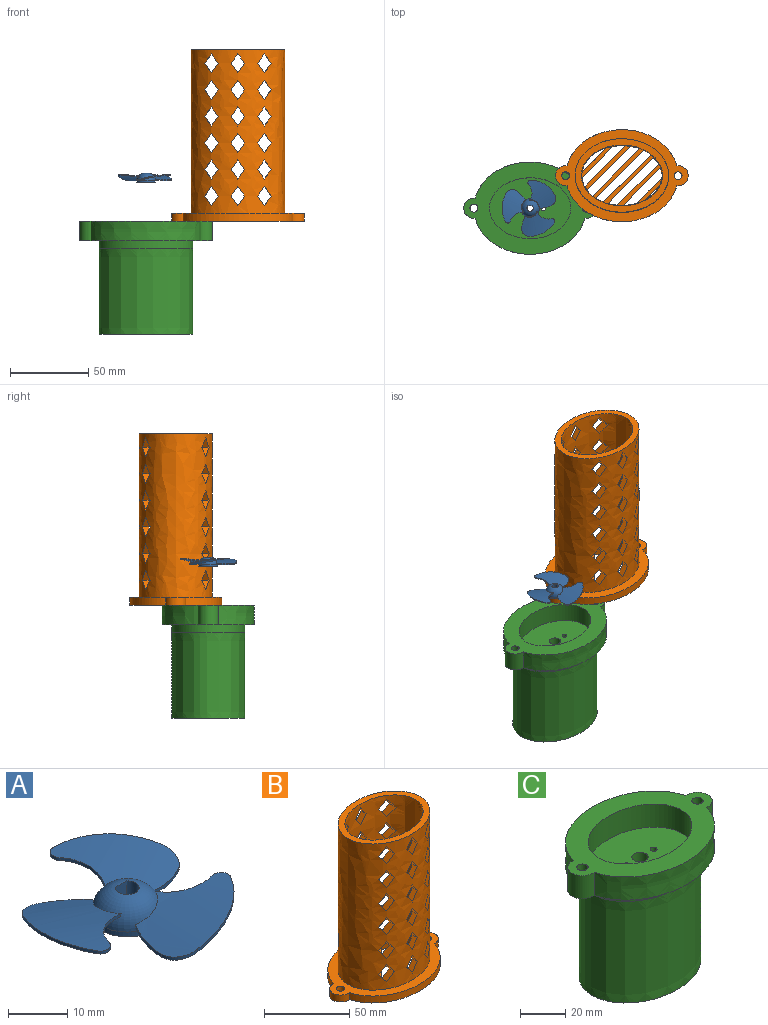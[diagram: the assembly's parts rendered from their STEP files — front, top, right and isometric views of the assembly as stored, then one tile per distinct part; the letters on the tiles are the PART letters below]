
ASSEMBLY  parts=3 mates=2
PART A: 26 faces, bbox 41.7x40.5x6 mm
  f0: cylinder r=72.3mm len=20.98mm, axis (0,-1,0), area 213.4mm2, adj f4,f5,f6,f7,f8,f23
  f1: cylinder r=71.7mm len=20.98mm, axis (0,-1,0), area 211mm2, adj f4,f5,f6,f7,f8,f23
  f2: cylinder r=6mm len=12mm, axis (0,0,-1), area 37.7mm2, adj f3,f23
  f3: plane 12x12mm, normal (0,0,-1), area 101.6mm2, adj f2,f24,f25
  f4: cylinder r=7.76mm len=9.01mm, axis (0,0,-1), area 6.5mm2, adj f0,f1,f8,f23
  f5: cylinder r=17.15mm len=8.45mm, axis (0,0,-1), area 5.5mm2, adj f0,f1,f6,f23
  f6: cylinder r=4.5mm len=4.53mm, axis (0,0,-1), area 4.3mm2, adj f0,f1,f5,f7
  f7: cylinder r=18mm len=16.51mm, axis (0,0,-1), area 11.9mm2, adj f0,f1,f6,f8
  f8: cylinder r=1.74mm len=2.64mm, axis (0,0,-1), area 2.5mm2, adj f0,f1,f4,f7
  f9: cylinder r=18mm len=18.61mm, axis (0,0,-1), area 11.9mm2, adj f10,f11,f14,f15
  f10: cylinder r=1.74mm len=3.19mm, axis (0,0,-1), area 2.5mm2, adj f9,f13,f14,f15
  f11: cylinder r=4.5mm len=6.04mm, axis (0,0,-1), area 4.3mm2, adj f9,f12,f14,f15
  f12: cylinder r=17.15mm len=6.23mm, axis (0,0,-1), area 5.5mm2, adj f11,f14,f15,f23
  f13: cylinder r=7.76mm len=8.49mm, axis (0,0,-1), area 6.5mm2, adj f10,f14,f15,f23
  f14: cylinder r=71.7mm len=25.87mm, axis (-0.87,0.5,0), area 211mm2, adj f9,f10,f11,f12,f13,f23
  f15: cylinder r=72.3mm len=26.1mm, axis (-0.87,0.5,0), area 213.4mm2, adj f9,f10,f11,f12,f13,f23
  f16: cylinder r=72.3mm len=26.1mm, axis (0.87,0.5,0), area 213.4mm2, adj f18,f19,f20,f21,f22,f23
  f17: cylinder r=71.7mm len=25.87mm, axis (0.87,0.5,0), area 211mm2, adj f18,f19,f20,f21,f22,f23
  f18: cylinder r=7.76mm len=10.11mm, axis (0,0,-1), area 6.5mm2, adj f16,f17,f22,f23
  f19: cylinder r=17.15mm len=8.48mm, axis (0,0,-1), area 5.5mm2, adj f16,f17,f20,f23
  f20: cylinder r=4.5mm len=5.92mm, axis (0,0,-1), area 4.3mm2, adj f16,f17,f19,f21
  f21: cylinder r=18mm len=15.73mm, axis (0,0,-1), area 11.9mm2, adj f16,f17,f20,f22
  f22: cylinder r=1.74mm len=2.93mm, axis (0,0,-1), area 2.5mm2, adj f16,f17,f18,f21
  f23: torus R=1mm, axis (0,0,1), area 180mm2, adj f0,f1,f2,f4,f5,f12,f13,f14
  f24: plane 5.98x2.76mm, normal (0,-1,0), area 16.4mm2, adj f3,f23,f25
  f25: cylinder r=2mm len=5.9mm, axis (0,0,-1), area 56.2mm2, adj f3,f23,f24
PART B: 193 faces, bbox 85.3x59.3x110.3 mm
  f0: plane 4.56x1.05mm, normal (0,0,-1), area 0mm2, adj f8,f172,f185
  f1: plane 4.25x3.38mm, normal (0,0,-1), area 0.2mm2, adj f8,f173,f174,f185
  f2: plane 4.96x2.58mm, normal (0,0,-1), area 0.1mm2, adj f8,f169,f170,f184
  f3: plane 4.7x2.93mm, normal (0,0,-1), area 0.2mm2, adj f8,f170,f171,f184
  f4: plane 3.89x3.75mm, normal (0,0,-1), area 0.2mm2, adj f8,f166,f167,f183
  f5: plane 5.96x1.65mm, normal (0,0,-1), area 0.1mm2, adj f8,f167,f168
  f6: plane 16.21x16.21mm, normal (0,0,-1), area 0.6mm2, adj f8,f162,f181
  f7: plane 10.43x10.43mm, normal (0,0,-1), area 0.4mm2, adj f8,f161,f190
  f8: extruded ~105x52mm, area 12884.8mm2, adj f0,f1,f2,f3,f4,f5,f6,f7
  f9: extruded ~105x60mm, area 15620.5mm2, adj f10,f11,f12,f13,f14,f15,f16,f17
  f10: plane 60x47mm, normal (0,0,1), area 624.8mm2, adj f8,f9
  f11: plane 6.17x4.33mm, normal (-0.82,0,-0.57), area 30.1mm2, adj f8,f9,f12,f14
  f12: plane 6.17x4.33mm, normal (-0.82,0,0.57), area 30.1mm2, adj f8,f9,f11,f13
  f13: plane 6.17x4.33mm, normal (0.82,0,0.57), area 30.1mm2, adj f8,f9,f12,f14
  f14: plane 6.17x4.33mm, normal (0.82,0,-0.57), area 30.1mm2, adj f8,f9,f11,f13
  f15: plane 6.17x4.33mm, normal (0.82,0,-0.57), area 30.1mm2, adj f8,f9,f16,f18
  f16: plane 6.17x4.33mm, normal (0.82,0,0.57), area 30.1mm2, adj f8,f9,f15,f17
  f17: plane 6.17x4.33mm, normal (-0.82,0,0.57), area 30.1mm2, adj f8,f9,f16,f18
  f18: plane 6.17x4.33mm, normal (-0.82,0,-0.57), area 30.1mm2, adj f8,f9,f15,f17
  f19: plane 6.17x4.33mm, normal (-0.82,0,0.57), area 30.1mm2, adj f8,f9,f20,f22
  f20: plane 6.17x4.33mm, normal (0.82,0,0.57), area 30.1mm2, adj f8,f9,f19,f21
  f21: plane 6.17x4.33mm, normal (0.82,0,-0.57), area 30.1mm2, adj f8,f9,f20,f22
  f22: plane 6.17x4.33mm, normal (-0.82,0,-0.57), area 30.1mm2, adj f8,f9,f19,f21
  f23: plane 6.17x4.33mm, normal (-0.82,0,-0.57), area 30.1mm2, adj f8,f9,f24,f26
  f24: plane 6.17x4.33mm, normal (0.82,0,-0.57), area 30.1mm2, adj f8,f9,f23,f25
  f25: plane 6.17x4.33mm, normal (0.82,0,0.57), area 30.1mm2, adj f8,f9,f24,f26
  f26: plane 6.17x4.33mm, normal (-0.82,0,0.57), area 30.1mm2, adj f8,f9,f23,f25
  f27: plane 8.56x6.47mm, normal (-0.82,0,-0.57), area 37.3mm2, adj f8,f9,f28,f30
  f28: plane 8.56x6.47mm, normal (-0.82,0,0.57), area 37.3mm2, adj f8,f9,f27,f29
  f29: plane 6.72x6.28mm, normal (0.82,0,0.57), area 33.4mm2, adj f8,f9,f28,f30
  f30: plane 6.72x6.28mm, normal (0.82,0,-0.57), area 33.4mm2, adj f8,f9,f27,f29
  f31: plane 6.72x6.28mm, normal (0.82,0,-0.57), area 33.4mm2, adj f8,f9,f32,f34
  f32: plane 6.72x6.28mm, normal (0.82,0,0.57), area 33.4mm2, adj f8,f9,f31,f33
  f33: plane 8.56x6.47mm, normal (-0.82,0,0.57), area 37.3mm2, adj f8,f9,f32,f34
  f34: plane 8.56x6.47mm, normal (-0.82,0,-0.57), area 37.3mm2, adj f8,f9,f31,f33
  f35: plane 6.17x4.33mm, normal (-0.82,0,0.57), area 30.1mm2, adj f8,f9,f36,f38
  f36: plane 6.17x4.33mm, normal (0.82,0,0.57), area 30.1mm2, adj f8,f9,f35,f37
  f37: plane 6.17x4.33mm, normal (0.82,0,-0.57), area 30.1mm2, adj f8,f9,f36,f38
  f38: plane 6.17x4.33mm, normal (-0.82,0,-0.57), area 30.1mm2, adj f8,f9,f35,f37
  f39: plane 6.17x4.33mm, normal (-0.82,0,-0.57), area 30.1mm2, adj f8,f9,f40,f42
  f40: plane 6.17x4.33mm, normal (0.82,0,-0.57), area 30.1mm2, adj f8,f9,f39,f41
  f41: plane 6.17x4.33mm, normal (0.82,0,0.57), area 30.1mm2, adj f8,f9,f40,f42
  f42: plane 6.17x4.33mm, normal (-0.82,0,0.57), area 30.1mm2, adj f8,f9,f39,f41
  f43: plane 6.72x6.28mm, normal (-0.82,0,0.57), area 33.4mm2, adj f8,f9,f44,f46
  f44: plane 8.56x6.47mm, normal (0.82,0,0.57), area 37.3mm2, adj f8,f9,f43,f45
  f45: plane 8.56x6.47mm, normal (0.82,0,-0.57), area 37.3mm2, adj f8,f9,f44,f46
  f46: plane 6.72x6.28mm, normal (-0.82,0,-0.57), area 33.4mm2, adj f8,f9,f43,f45
  f47: plane 6.72x6.28mm, normal (-0.82,0,-0.57), area 33.4mm2, adj f8,f9,f48,f50
  f48: plane 8.56x6.47mm, normal (0.82,0,-0.57), area 37.3mm2, adj f8,f9,f47,f49
  f49: plane 8.56x6.47mm, normal (0.82,0,0.57), area 37.3mm2, adj f8,f9,f48,f50
  f50: plane 6.72x6.28mm, normal (-0.82,0,0.57), area 33.4mm2, adj f8,f9,f47,f49
  f51: plane 8.56x6.47mm, normal (-0.82,0,-0.57), area 37.3mm2, adj f8,f9,f52,f54
  f52: plane 8.56x6.47mm, normal (-0.82,0,0.57), area 37.3mm2, adj f8,f9,f51,f53
  f53: plane 6.72x6.28mm, normal (0.82,0,0.57), area 33.4mm2, adj f8,f9,f52,f54
  f54: plane 6.72x6.28mm, normal (0.82,0,-0.57), area 33.4mm2, adj f8,f9,f51,f53
  f55: plane 6.72x6.28mm, normal (0.82,0,-0.57), area 33.4mm2, adj f8,f9,f56,f58
  f56: plane 6.72x6.28mm, normal (0.82,0,0.57), area 33.4mm2, adj f8,f9,f55,f57
  f57: plane 8.56x6.47mm, normal (-0.82,0,0.57), area 37.3mm2, adj f8,f9,f56,f58
  f58: plane 8.56x6.47mm, normal (-0.82,0,-0.57), area 37.3mm2, adj f8,f9,f55,f57
  f59: plane 6.72x6.28mm, normal (-0.82,0,0.57), area 33.4mm2, adj f8,f9,f60,f62
  f60: plane 8.56x6.47mm, normal (0.82,0,0.57), area 37.3mm2, adj f8,f9,f59,f61
  f61: plane 8.56x6.47mm, normal (0.82,0,-0.57), area 37.3mm2, adj f8,f9,f60,f62
  f62: plane 6.72x6.28mm, normal (-0.82,0,-0.57), area 33.4mm2, adj f8,f9,f59,f61
  f63: plane 6.72x6.28mm, normal (-0.82,0,-0.57), area 33.4mm2, adj f8,f9,f64,f66
  f64: plane 8.56x6.47mm, normal (0.82,0,-0.57), area 37.3mm2, adj f8,f9,f63,f65
  f65: plane 8.56x6.47mm, normal (0.82,0,0.57), area 37.3mm2, adj f8,f9,f64,f66
  f66: plane 6.72x6.28mm, normal (-0.82,0,0.57), area 33.4mm2, adj f8,f9,f63,f65
  f67: plane 6.17x4.33mm, normal (-0.82,0,0.57), area 30.1mm2, adj f8,f9,f68,f70
  f68: plane 6.17x4.33mm, normal (0.82,0,0.57), area 30.1mm2, adj f8,f9,f67,f69
  f69: plane 6.17x4.33mm, normal (0.82,0,-0.57), area 30.1mm2, adj f8,f9,f68,f70
  f70: plane 6.17x4.33mm, normal (-0.82,0,-0.57), area 30.1mm2, adj f8,f9,f67,f69
  f71: plane 6.17x4.33mm, normal (-0.82,0,-0.57), area 30.1mm2, adj f8,f9,f72,f74
  f72: plane 6.17x4.33mm, normal (0.82,0,-0.57), area 30.1mm2, adj f8,f9,f71,f73
  f73: plane 6.17x4.33mm, normal (0.82,0,0.57), area 30.1mm2, adj f8,f9,f72,f74
  f74: plane 6.17x4.33mm, normal (-0.82,0,0.57), area 30.1mm2, adj f8,f9,f71,f73
  f75: plane 8.56x6.47mm, normal (-0.82,0,-0.57), area 37.3mm2, adj f8,f9,f76,f78
  f76: plane 8.56x6.47mm, normal (-0.82,0,0.57), area 37.3mm2, adj f8,f9,f75,f77
  f77: plane 6.72x6.28mm, normal (0.82,0,0.57), area 33.4mm2, adj f8,f9,f76,f78
  f78: plane 6.72x6.28mm, normal (0.82,0,-0.57), area 33.4mm2, adj f8,f9,f75,f77
  f79: plane 6.72x6.28mm, normal (0.82,0,-0.57), area 33.4mm2, adj f8,f9,f80,f82
  f80: plane 6.72x6.28mm, normal (0.82,0,0.57), area 33.4mm2, adj f8,f9,f79,f81
  f81: plane 8.56x6.47mm, normal (-0.82,0,0.57), area 37.3mm2, adj f8,f9,f80,f82
  f82: plane 8.56x6.47mm, normal (-0.82,0,-0.57), area 37.3mm2, adj f8,f9,f79,f81
  f83: plane 6.72x6.28mm, normal (-0.82,0,0.57), area 33.4mm2, adj f8,f9,f84,f86
  f84: plane 8.56x6.47mm, normal (0.82,0,0.57), area 37.3mm2, adj f8,f9,f83,f85
  f85: plane 8.56x6.47mm, normal (0.82,0,-0.57), area 37.3mm2, adj f8,f9,f84,f86
  f86: plane 6.72x6.28mm, normal (-0.82,0,-0.57), area 33.4mm2, adj f8,f9,f83,f85
  f87: plane 6.72x6.28mm, normal (-0.82,0,-0.57), area 33.4mm2, adj f8,f9,f88,f90
  f88: plane 8.56x6.47mm, normal (0.82,0,-0.57), area 37.3mm2, adj f8,f9,f87,f89
  f89: plane 8.56x6.47mm, normal (0.82,0,0.57), area 37.3mm2, adj f8,f9,f88,f90
  f90: plane 6.72x6.28mm, normal (-0.82,0,0.57), area 33.4mm2, adj f8,f9,f87,f89
  f91: plane 8.56x6.47mm, normal (0.82,0,0.57), area 37.3mm2, adj f8,f9,f92,f94
  f92: plane 8.56x6.47mm, normal (0.82,0,-0.57), area 37.3mm2, adj f8,f9,f91,f93
  f93: plane 6.72x6.28mm, normal (-0.82,0,-0.57), area 33.4mm2, adj f8,f9,f92,f94
  f94: plane 6.72x6.28mm, normal (-0.82,0,0.57), area 33.4mm2, adj f8,f9,f91,f93
  f95: plane 6.72x6.28mm, normal (-0.82,0,0.57), area 33.4mm2, adj f8,f9,f96,f98
  f96: plane 6.72x6.28mm, normal (-0.82,0,-0.57), area 33.4mm2, adj f8,f9,f95,f97
  f97: plane 8.56x6.47mm, normal (0.82,0,-0.57), area 37.3mm2, adj f8,f9,f96,f98
  f98: plane 8.56x6.47mm, normal (0.82,0,0.57), area 37.3mm2, adj f8,f9,f95,f97
  f99: plane 8.56x6.47mm, normal (-0.82,0,-0.57), area 37.3mm2, adj f8,f9,f100,f102
  f100: plane 8.56x6.47mm, normal (-0.82,0,0.57), area 37.3mm2, adj f8,f9,f99,f101
  f101: plane 6.72x6.28mm, normal (0.82,0,0.57), area 33.4mm2, adj f8,f9,f100,f102
  f102: plane 6.72x6.28mm, normal (0.82,0,-0.57), area 33.4mm2, adj f8,f9,f99,f101
  f103: plane 6.72x6.28mm, normal (0.82,0,-0.57), area 33.4mm2, adj f8,f9,f104,f106
  f104: plane 6.72x6.28mm, normal (0.82,0,0.57), area 33.4mm2, adj f8,f9,f103,f105
  f105: plane 8.56x6.47mm, normal (-0.82,0,0.57), area 37.3mm2, adj f8,f9,f104,f106
  f106: plane 8.56x6.47mm, normal (-0.82,0,-0.57), area 37.3mm2, adj f8,f9,f103,f105
  f107: plane 8.56x6.47mm, normal (-0.82,0,-0.57), area 37.3mm2, adj f8,f9,f108,f110
  f108: plane 8.56x6.47mm, normal (-0.82,0,0.57), area 37.3mm2, adj f8,f9,f107,f109
  f109: plane 6.72x6.28mm, normal (0.82,0,0.57), area 33.4mm2, adj f8,f9,f108,f110
  f110: plane 6.72x6.28mm, normal (0.82,0,-0.57), area 33.4mm2, adj f8,f9,f107,f109
  f111: plane 6.72x6.28mm, normal (0.82,0,-0.57), area 33.4mm2, adj f8,f9,f112,f114
  f112: plane 6.72x6.28mm, normal (0.82,0,0.57), area 33.4mm2, adj f8,f9,f111,f113
  f113: plane 8.56x6.47mm, normal (-0.82,0,0.57), area 37.3mm2, adj f8,f9,f112,f114
  f114: plane 8.56x6.47mm, normal (-0.82,0,-0.57), area 37.3mm2, adj f8,f9,f111,f113
  f115: plane 6.72x6.28mm, normal (-0.82,0,0.57), area 33.4mm2, adj f8,f9,f116,f118
  f116: plane 8.56x6.47mm, normal (0.82,0,0.57), area 37.3mm2, adj f8,f9,f115,f117
  f117: plane 8.56x6.47mm, normal (0.82,0,-0.57), area 37.3mm2, adj f8,f9,f116,f118
  f118: plane 6.72x6.28mm, normal (-0.82,0,-0.57), area 33.4mm2, adj f8,f9,f115,f117
  f119: plane 6.72x6.28mm, normal (-0.82,0,-0.57), area 33.4mm2, adj f8,f9,f120,f122
  f120: plane 8.56x6.47mm, normal (0.82,0,-0.57), area 37.3mm2, adj f8,f9,f119,f121
  f121: plane 8.56x6.47mm, normal (0.82,0,0.57), area 37.3mm2, adj f8,f9,f120,f122
  f122: plane 6.72x6.28mm, normal (-0.82,0,0.57), area 33.4mm2, adj f8,f9,f119,f121
  f123: plane 6.17x4.33mm, normal (-0.82,0,0.57), area 30.1mm2, adj f8,f9,f124,f126
  f124: plane 6.17x4.33mm, normal (0.82,0,0.57), area 30.1mm2, adj f8,f9,f123,f125
  f125: plane 6.17x4.33mm, normal (0.82,0,-0.57), area 30.1mm2, adj f8,f9,f124,f126
  f126: plane 6.17x4.33mm, normal (-0.82,0,-0.57), area 30.1mm2, adj f8,f9,f123,f125
  f127: plane 6.17x4.33mm, normal (-0.82,0,-0.57), area 30.1mm2, adj f8,f9,f128,f130
  f128: plane 6.17x4.33mm, normal (0.82,0,-0.57), area 30.1mm2, adj f8,f9,f127,f129
  f129: plane 6.17x4.33mm, normal (0.82,0,0.57), area 30.1mm2, adj f8,f9,f128,f130
  f130: plane 6.17x4.33mm, normal (-0.82,0,0.57), area 30.1mm2, adj f8,f9,f127,f129
  f131: plane 6.72x6.28mm, normal (-0.82,0,0.57), area 33.4mm2, adj f8,f9,f132,f134
  f132: plane 8.56x6.47mm, normal (0.82,0,0.57), area 37.3mm2, adj f8,f9,f131,f133
  f133: plane 8.56x6.47mm, normal (0.82,0,-0.57), area 37.3mm2, adj f8,f9,f132,f134
  f134: plane 6.72x6.28mm, normal (-0.82,0,-0.57), area 33.4mm2, adj f8,f9,f131,f133
  f135: plane 6.72x6.28mm, normal (-0.82,0,-0.57), area 33.4mm2, adj f8,f9,f136,f138
  f136: plane 8.56x6.47mm, normal (0.82,0,-0.57), area 37.3mm2, adj f8,f9,f135,f137
  f137: plane 8.56x6.47mm, normal (0.82,0,0.57), area 37.3mm2, adj f8,f9,f136,f138
  f138: plane 6.72x6.28mm, normal (-0.82,0,0.57), area 33.4mm2, adj f8,f9,f135,f137
  f139: plane 8.56x6.47mm, normal (-0.82,0,-0.57), area 37.3mm2, adj f8,f9,f140,f142
  f140: plane 8.56x6.47mm, normal (-0.82,0,0.57), area 37.3mm2, adj f8,f9,f139,f141
  f141: plane 6.72x6.28mm, normal (0.82,0,0.57), area 33.4mm2, adj f8,f9,f140,f142
  f142: plane 6.72x6.28mm, normal (0.82,0,-0.57), area 33.4mm2, adj f8,f9,f139,f141
  f143: plane 6.72x6.28mm, normal (0.82,0,-0.57), area 33.4mm2, adj f8,f9,f144,f146
  f144: plane 6.72x6.28mm, normal (0.82,0,0.57), area 33.4mm2, adj f8,f9,f143,f145
  f145: plane 8.56x6.47mm, normal (-0.82,0,0.57), area 37.3mm2, adj f8,f9,f144,f146
  f146: plane 8.56x6.47mm, normal (-0.82,0,-0.57), area 37.3mm2, adj f8,f9,f143,f145
  f147: plane 6.17x4.33mm, normal (-0.82,0,0.57), area 30.1mm2, adj f8,f9,f148,f150
  f148: plane 6.17x4.33mm, normal (0.82,0,0.57), area 30.1mm2, adj f8,f9,f147,f149
  f149: plane 6.17x4.33mm, normal (0.82,0,-0.57), area 30.1mm2, adj f8,f9,f148,f150
  f150: plane 6.17x4.33mm, normal (-0.82,0,-0.57), area 30.1mm2, adj f8,f9,f147,f149
  f151: plane 6.17x4.33mm, normal (-0.82,0,-0.57), area 30.1mm2, adj f8,f9,f152,f154
  f152: plane 6.17x4.33mm, normal (0.82,0,-0.57), area 30.1mm2, adj f8,f9,f151,f153
  f153: plane 6.17x4.33mm, normal (0.82,0,0.57), area 30.1mm2, adj f8,f9,f152,f154
  f154: plane 6.17x4.33mm, normal (-0.82,0,0.57), area 30.1mm2, adj f8,f9,f151,f153
  f155: plane 28.24x27.24mm, normal (0,0,1), area 92mm2, adj f8,f173,f186
  f156: plane 32.67x31.69mm, normal (0,0,1), area 107.6mm2, adj f8,f170,f185
  f157: plane 33.12x32.14mm, normal (0,0,1), area 109.2mm2, adj f8,f167,f184
  f158: plane 29.82x28.82mm, normal (0,0,1), area 97.5mm2, adj f8,f164,f183
  f159: plane 20.8x20.67mm, normal (0,0,1), area 65.4mm2, adj f8,f181,f182
  f160: plane 17.2x17.2mm, normal (0,0,1), area 49.9mm2, adj f8,f161,f176
  f161: plane 10.38x10.38mm, normal (0.71,-0.71,0), area 73.4mm2, adj f7,f160,f190,f191
  f162: extruded ~16.03x16.03mm, area 119.5mm2, adj f6,f181,f191
  f163: extruded ~5.68x5mm, area 30mm2, adj f8,f164,f182,f191
  f164: plane 26.66x26.66mm, normal (-0.71,0.71,0), area 188.5mm2, adj f158,f163,f165,f191
  f165: extruded ~7.78x5mm, area 39mm2, adj f8,f164,f182,f191
  f166: extruded ~5x3.81mm, area 26.5mm2, adj f4,f167,f183,f191
  f167: plane 30.68x30.68mm, normal (-0.71,0.71,0), area 217mm2, adj f4,f5,f157,f166,f168,f191
  f168: extruded ~5.9x5mm, area 30.6mm2, adj f5,f167,f183,f191
  f169: extruded ~5x4.93mm, area 27.8mm2, adj f2,f170,f184,f191
  f170: plane 30.81x30.81mm, normal (-0.71,0.71,0), area 217.9mm2, adj f2,f3,f156,f169,f171,f191
  f171: extruded ~5x4.62mm, area 27.2mm2, adj f3,f170,f184,f191
  f172: extruded ~6.27x5mm, area 32mm2, adj f0,f8,f173,f185,f191
  f173: plane 27.09x27.09mm, normal (-0.71,0.71,0), area 191.6mm2, adj f1,f155,f172,f174,f191
  f174: extruded ~5x4.18mm, area 26.7mm2, adj f1,f173,f185,f191
  f175: extruded ~8.6x5mm, area 43.5mm2, adj f8,f176,f186,f191
  f176: plane 17.2x17.2mm, normal (-0.71,0.71,0), area 121.6mm2, adj f160,f175,f177,f191
  f177: extruded ~6.51x5mm, area 33.2mm2, adj f8,f176,f186,f191
  f178: cylinder r=6.5mm len=13mm, axis (0,0,1), area 110.7mm2, adj f179,f187,f191,f192
  f179: extruded ~70.29x23.06mm, area 451.1mm2, adj f178,f180,f191,f192
  f180: cylinder r=6.5mm len=13mm, axis (0,0,1), area 110.7mm2, adj f179,f187,f191,f192
  f181: plane 16.03x16.03mm, normal (-0.71,0.71,0), area 113.3mm2, adj f6,f159,f162,f191
  f182: plane 20.66x20.66mm, normal (0.71,-0.71,0), area 146.1mm2, adj f159,f163,f165,f191
  f183: plane 28.45x28.45mm, normal (0.71,-0.71,0), area 201.1mm2, adj f4,f158,f166,f168,f191
  f184: plane 31.12x31.12mm, normal (0.71,-0.71,0), area 220mm2, adj f2,f3,f157,f169,f171,f191
  f185: plane 30.07x30.07mm, normal (0.71,-0.71,0), area 212.7mm2, adj f0,f1,f156,f172,f174,f191
  f186: plane 24.85x24.85mm, normal (0.71,-0.71,0), area 175.7mm2, adj f155,f175,f177,f191
  f187: extruded ~70.29x23.06mm, area 451.1mm2, adj f178,f180,f191,f192
  f188: cylinder r=2.5mm len=5mm, axis (0,0,1), area 78.5mm2, adj f191,f192
  f189: cylinder r=2.5mm len=5mm, axis (0,0,1), area 78.5mm2, adj f191,f192
  f190: extruded ~10.38x10.38mm, area 74.9mm2, adj f7,f161,f191
  f191: plane 85x59.01mm, normal (0,0,-1), area 2373.9mm2, adj f161,f162,f163,f164,f165,f166,f167,f168
  f192: plane 85x59.01mm, normal (0,0,1), area 1229.8mm2, adj f9,f178,f179,f180,f187,f188,f189
PART C: 22 faces, bbox 85x59x72.5 mm
  f0: plane 25x25mm, normal (0,0,-1), area 435mm2, adj f11,f12,f14,f20
  f1: cylinder r=6.5mm len=13mm, axis (0,0,1), area 276.7mm2, adj f2,f7,f8,f9
  f2: extruded ~70.29x23.06mm, area 1127.8mm2, adj f1,f3,f8,f9
  f3: cylinder r=6.5mm len=13mm, axis (0,0,1), area 276.7mm2, adj f2,f7,f8,f9
  f4: extruded ~52x39mm, area 1795.9mm2, adj f9,f10
  f5: cylinder r=2.5mm len=12.5mm, axis (0,0,1), area 196.3mm2, adj f8,f9
  f6: cylinder r=2.5mm len=12.5mm, axis (0,0,1), area 196.3mm2, adj f8,f9
  f7: extruded ~70.29x23.06mm, area 1127.8mm2, adj f1,f3,f8,f9
  f8: plane 85x59.01mm, normal (0,0,-1), area 1229.8mm2, adj f1,f2,f3,f5,f6,f7,f13
  f9: plane 85x59.01mm, normal (0,0,1), area 1851.8mm2, adj f1,f2,f3,f4,f5,f6,f7
  f10: plane 52x39mm, normal (0,0,1), area 1536.9mm2, adj f4,f11,f12,f14
  f11: cylinder r=1.53mm len=5mm, axis (0,0,1), area 47.9mm2, adj f0,f10
  f12: cylinder r=3.62mm len=7.25mm, axis (0,0,1), area 113.9mm2, adj f0,f10
  f13: extruded ~60x47mm, area 843.5mm2, adj f8,f15,f16,f17,f18
  f14: cylinder r=1.53mm len=5mm, axis (0,0,1), area 47.9mm2, adj f0,f10
  f15: plane 30.01x23.51mm, normal (0,0,1), area 0.7mm2, adj f13,f19
  f16: plane 30.01x23.51mm, normal (0,0,1), area 0.7mm2, adj f13,f19
  f17: plane 30.01x23.51mm, normal (0,0,1), area 0.7mm2, adj f13,f19
  f18: plane 30.01x23.51mm, normal (0,0,1), area 0.7mm2, adj f13,f19
  f19: extruded ~60x55mm, area 9284.7mm2, adj f15,f16,f17,f18,f21
  f20: cylinder r=12.5mm len=55mm, axis (0,0,1), area 4319.7mm2, adj f0,f21
  f21: plane 60x47mm, normal (0,0,-1), area 1726.6mm2, adj f19,f20
PLACE A t=(0.61,-47.62,104.02)mm
PLACE B t=(59.41,-26.82,81.17)mm
PLACE C t=(0.61,-47.62,76.17)mm
MATE planar B.f191 <-> C.f9  axis (0,0,1) through (59.41,2.68,76.17)mm
MATE cylindrical A.f2 <-> C.f12  axis (0,0,-1) through (0.61,-47.62,101.52)mm
